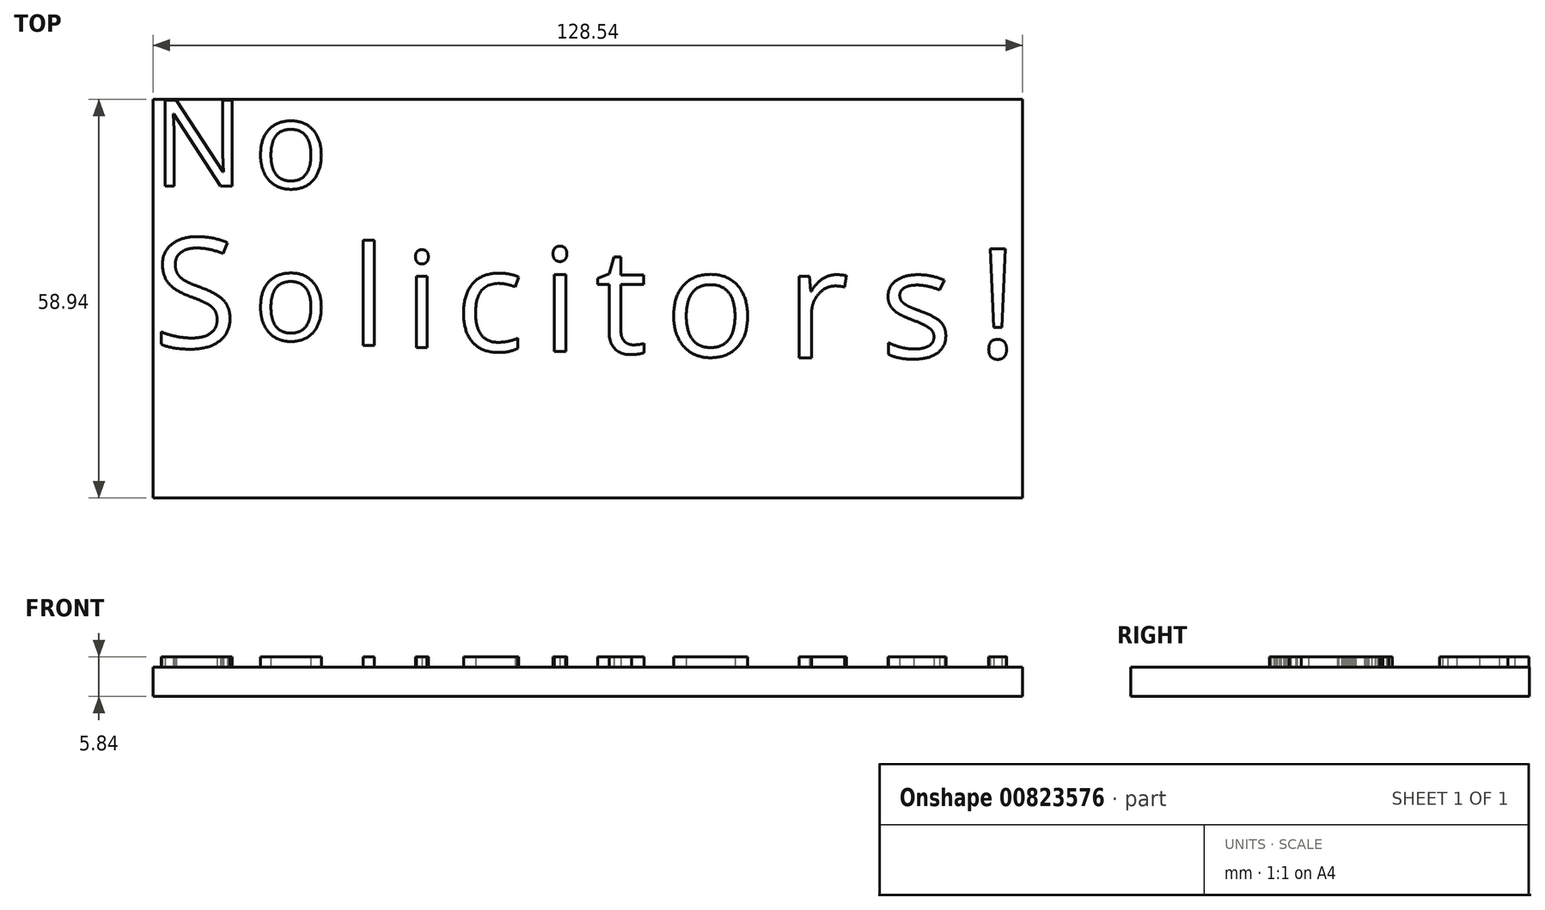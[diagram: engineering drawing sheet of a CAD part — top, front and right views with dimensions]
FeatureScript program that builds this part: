
annotation { "Feature Type Name" : "Feature", "Feature Type Description" : "" }
export const myFeature = defineFeature(function(context is Context, id is Id, definition is map)
    precondition{}
    {
        {
            var Q0;
            Q0=qCreatedBy(makeId("Top.planeOp"),FACE);
            var sketch = newSketch(context, id + "F0", { "sketchPlane" : qUnion([Q0])});
            skLineSegment(sketch, "E0.bottom", {"start": v(-62.35, 32.53) * mm, "end": v(66.2, 32.53) * mm});
            skLineSegment(sketch, "E0.top", {"start": v(-62.35, -26.4) * mm, "end": v(66.2, -26.4) * mm});
            skLineSegment(sketch, "E0.left", {"start": v(-62.35, 32.53) * mm, "end": v(-62.35, -26.4) * mm});
            skLineSegment(sketch, "E0.right", {"start": v(66.2, 32.53) * mm, "end": v(66.2, -26.4) * mm});
            skSolve(sketch);
        }
        {
            var Q0;
            Q0 = qSketchRegion(id + "F0", true);
            extrude(context, id + "F1", {"entities" : qUnion([Q0]), "oppositeDirection" : true, "depth" : 4.32 * mm, "offsetDistance" : 25.4 * mm});
        }
        {
            var Q0;
            Q0=makeQuery(id+"F1.opExtrude","CAP_FACE",FACE,{"disambiguationData":[OSD([sQuery(id+"F0.wireOp",EDGE,"E0.bottom"),sQuery(id+"F0.wireOp",EDGE,"E0.top"),sQuery(id+"F0.wireOp",EDGE,"E0.left"),sQuery(id+"F0.wireOp",EDGE,"E0.right")])],"isStart":true});
            var sketch = newSketch(context, id + "F2", { "sketchPlane" : qUnion([Q0])});
            skText(sketch, "E1", { "text": "N", "fontName": "OpenSans-Regular.ttf"});
            skText(sketch, "E2", { "text": "o", "fontName": "OpenSans-Regular.ttf"});
            skPoint(sketch, "E3.firstSnap0", {"position": v(-62.35, 3.06) * mm});
            skText(sketch, "E4", { "text": "S", "fontName": "OpenSans-Regular.ttf"});
            skText(sketch, "E5", { "text": "o", "fontName": "OpenSans-Regular.ttf"});
            skText(sketch, "E6", { "text": "l", "fontName": "OpenSans-Regular.ttf"});
            skText(sketch, "E7", { "text": "i", "fontName": "OpenSans-Regular.ttf"});
            skText(sketch, "E8", { "text": "c", "fontName": "OpenSans-Regular.ttf"});
            skText(sketch, "E9", { "text": "i", "fontName": "OpenSans-Regular.ttf"});
            skText(sketch, "E10", { "text": "t", "fontName": "OpenSans-Regular.ttf"});
            skText(sketch, "E11", { "text": "o", "fontName": "OpenSans-Regular.ttf"});
            skText(sketch, "E12", { "text": "r", "fontName": "OpenSans-Regular.ttf"});
            skText(sketch, "E13", { "text": "s", "fontName": "OpenSans-Regular.ttf"});
            skText(sketch, "E14", { "text": "!", "fontName": "OpenSans-Regular.ttf"});
            const initialGuessF2  = {"E1": [-0.06235, 0.0197, 1, 0, 0.01282], "E2": [-0.04749, 0.01939, 1, 0, 0.01314], "E4": [-0.06235, -0.0042, 1, 0, 0.01633], "E5": [-0.04749, -0.00311, 1, 0, 0.01314], "E6": [-0.03309, -0.00385, 1, 0, 0.01475], "E7": [-0.02512, -0.00421, 1, 0, 0.01424], "E8": [-0.01765, -0.0047, 1, 0, 0.01523], "E9": [-0.0049, -0.00476, 1, 0, 0.01529], "E10": [0.00307, -0.00502, 1, 0, 0.01555], "E11": [0.01336, -0.00547, 1, 0, 0.016], "E12": [0.03122, -0.0057, 1, 0, 0.01624], "E13": [0.04513, -0.00569, 1, 0, 0.01622], "E14": [0.05952, -0.00562, 1, 0, 0.01615]};
            skSetInitialGuess(sketch, initialGuessF2);
            skSolve(sketch);
        }
        {
            var Q0;
            Q0 = qSketchRegion(id + "F2", true);
            extrude(context, id + "F3", {"entities" : qUnion([Q0]), "operationType" : NewBodyOperationType.ADD, "depth" : 1.52 * mm, "offsetDistance" : 25.4 * mm});
        }
    });
